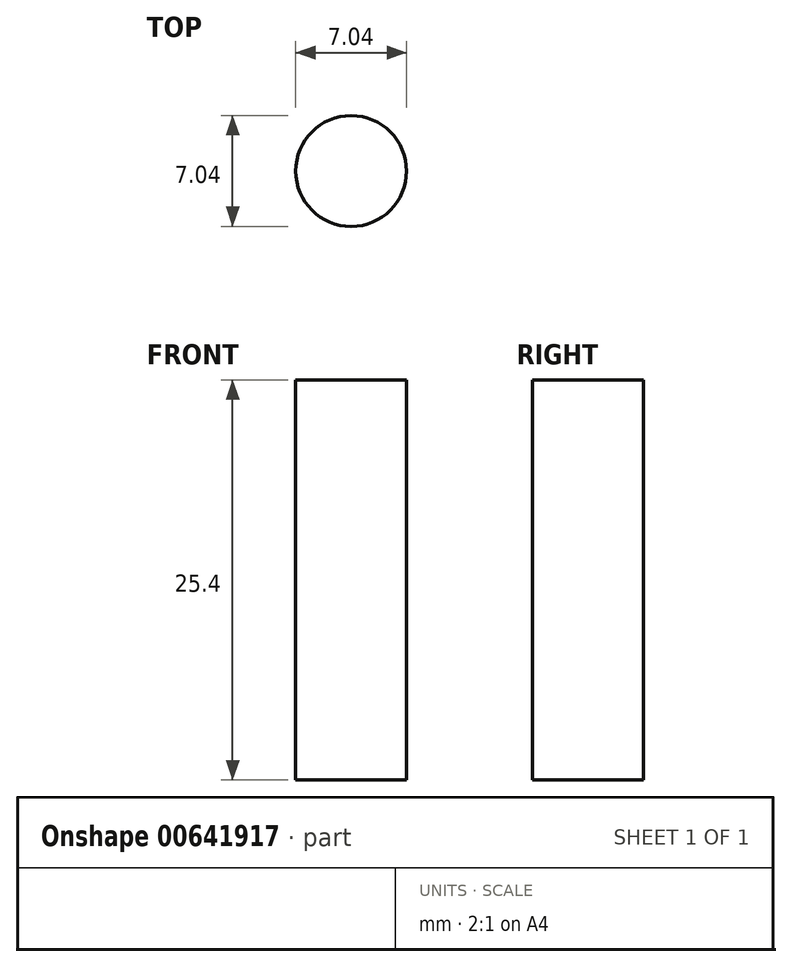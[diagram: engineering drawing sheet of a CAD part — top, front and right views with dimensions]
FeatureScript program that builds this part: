
annotation { "Feature Type Name" : "Feature", "Feature Type Description" : "" }
export const myFeature = defineFeature(function(context is Context, id is Id, definition is map)
    precondition{}
    {
        {
            var Q0;
            Q0=qCreatedBy(makeId("Top.planeOp"),FACE);
            var sketch = newSketch(context, id + "F0", { "sketchPlane" : qUnion([Q0])});
            skCircle(sketch, "E0", {"center": v(0, 0) * mm, "radius": 3.52 * mm});
            skSolve(sketch);
        }
        {
            var Q0;
            Q0 = qSketchRegion(id + "F0", true);
            extrude(context, id + "F1", {"entities" : qUnion([Q0]), "depth" : 25.4 * mm, "offsetDistance" : 25.4 * mm});
        }
    });
